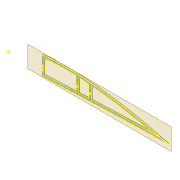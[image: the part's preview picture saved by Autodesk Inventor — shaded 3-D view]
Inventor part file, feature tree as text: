
AUTODESK INVENTOR PART (.ipt)
format: ipt  version: 2022 (Build 260153000, 153)  size: 360,960 bytes
history: native  units: mm
features: extrude x6, sketch x6, projected_geometry x5, shell x1, fillet x1, plane x1
ambient origin geometry x8: Origin, YZ Plane, XZ Plane, XY Plane, X Axis, Y Axis, Z Axis, Center Point
bodies: Solid1 (feature_tree)
feature tree (20):
  extrude  "Extrusion1"  Depth=4.0mm
  shell  "Shell1"  Thickness=5.0mm
  extrude  "Extrusion2"  Depth=2.0mm
  extrude  "Extrusion3"  Depth=5.9mm
  extrude  "Extrusion4"  Depth=10.0mm TaperAngle=0.0deg
  fillet  "Fillet1"  Radius=65.0mm
  extrude  "Extrusion5"  Depth=2.0mm TaperAngle=0.0deg
  plane  "Work Plane2"
  extrude  "Extrusion8"  Depth=0.5mm
  sketch  "Sketch17"  dims[d31=2.0mm d32=5.0mm d34=1.6mm d35=2.5mm d37=5.0mm d38=1.6mm d40=2.5mm d41=65.0mm d42=20.0mm d43=0.5mm d44=10.0mm d45=0.0mm d46=2.5mm d47=2.5mm]
  sketch  "Sketch3"  dims[d0=2.0mm d1=0.0mm d2=4.0mm d3=5.0mm]
  projected_geometry  "Projected Loop3"
  sketch  "Sketch8"  dims[d5=2.0mm d6=0.0mm d7=2.0mm]
  sketch  "Sketch9"  dims[d8=2.0mm d9=5.9mm]
  sketch  "Sketch10"  dims[d12=8.0mm d13=10.0mm d14=0.0mm d15=65.0mm]
  projected_geometry  "Projected Loop4"
  projected_geometry  "Projected Loop10"
  sketch  "Sketch16"  dims[d16=10.0mm d17=0.0mm d22=2.0mm d23=0.0mm]
  projected_geometry  "Projected Loop11"
  projected_geometry  "Project Cut Edges1"
